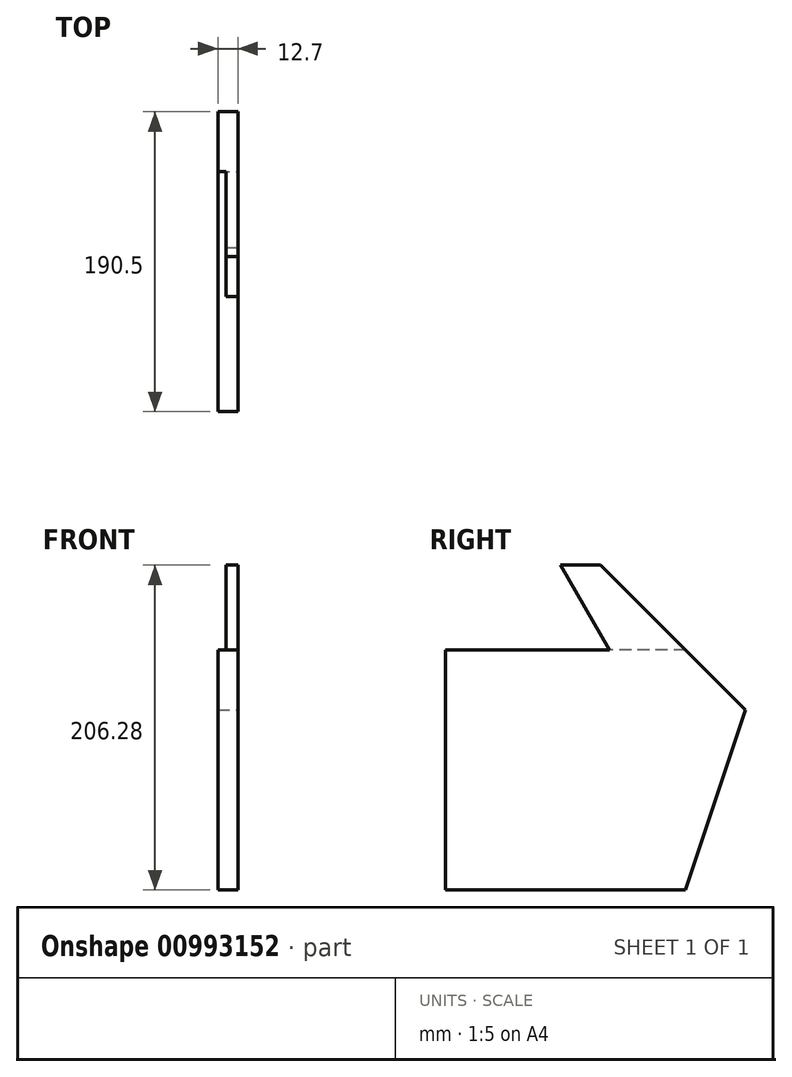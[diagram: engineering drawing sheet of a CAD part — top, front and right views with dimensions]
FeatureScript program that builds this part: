
annotation { "Feature Type Name" : "Feature", "Feature Type Description" : "" }
export const myFeature = defineFeature(function(context is Context, id is Id, definition is map)
    precondition{}
    {
        {
            var Q0;
            Q0=qCreatedBy(makeId("Right.planeOp"),FACE);
            var sketch = newSketch(context, id + "F0", { "sketchPlane" : qUnion([Q0])});
            skLineSegment(sketch, "E0.bottom", {"start": v(-23.56, 53.88) * mm, "end": v(-175.96, 53.88) * mm});
            skLineSegment(sketch, "E0.top", {"start": v(-23.56, -98.52) * mm, "end": v(-175.96, -98.52) * mm});
            skLineSegment(sketch, "E0.left", {"start": v(-23.56, 53.88) * mm, "end": v(-23.56, -98.52) * mm});
            skLineSegment(sketch, "E0.right", {"start": v(-175.96, 53.88) * mm, "end": v(-175.96, -98.52) * mm});
            skLineSegment(sketch, "E1", {"start": v(-23.56, 53.88) * mm, "end": v(-77.45, 107.76) * mm});
            skLineSegment(sketch, "E2", {"start": v(-77.45, 107.76) * mm, "end": v(-102.85, 107.76) * mm});
            skLineSegment(sketch, "E3", {"start": v(-102.85, 107.76) * mm, "end": v(-71.74, 53.88) * mm});
            skLineSegment(sketch, "E4", {"start": v(-23.56, 53.88) * mm, "end": v(14.54, 15.78) * mm});
            skLineSegment(sketch, "E5", {"start": v(14.54, 15.78) * mm, "end": v(-23.56, 15.78) * mm});
            skLineSegment(sketch, "E6", {"start": v(14.54, 15.78) * mm, "end": v(-23.56, -98.52) * mm});
            skSolve(sketch);
        }
        {
            var Q0;
            Q0=makeQuery(id+"F0.imprint","IMPRINT",FACE,{"disambiguationData":[TD([[makeQuery(id+"F0.imprint","IMPRINT",EDGE,{"derivedFrom":sQuery(id+"F0.wireOp",EDGE,"E0.top")}),-1.0]])]});
            var Q1;
            {var subQ0=sQuery(id+"F0.wireOp",EDGE,"E4");Q1=makeQuery(id+"F0.imprint","IMPRINT",FACE,{"disambiguationData":[TD([[makeQuery(id+"F0.imprint","IMPRINT",EDGE,{"derivedFrom":subQ0}),-1.0]])]});}
            var Q2;
            {var subQ2=sQuery(id+"F0.wireOp",EDGE,"E5");Q2=makeQuery(id+"F0.imprint","IMPRINT",FACE,{"disambiguationData":[TD([[makeQuery(id+"F0.imprint","IMPRINT",EDGE,{"derivedFrom":subQ2}),1.0]])]});}
            extrude(context, id + "F1", {"entities" : qUnion([Q0, Q1, Q2]), "oppositeDirection" : true, "depth" : 12.7 * mm, "offsetDistance" : 25.4 * mm});
        }
        {
            var Q0;
            {var subQ0=sQuery(id+"F0.wireOp",EDGE,"E1");Q0=makeQuery(id+"F0.imprint","IMPRINT",FACE,{"disambiguationData":[TD([[makeQuery(id+"F0.imprint","IMPRINT",EDGE,{"derivedFrom":subQ0}),1.0]])]});}
            extrude(context, id + "F2", {"entities" : qUnion([Q0]), "operationType" : NewBodyOperationType.ADD, "oppositeDirection" : true, "depth" : 7.62 * mm, "offsetDistance" : 25.4 * mm});
        }
    });
